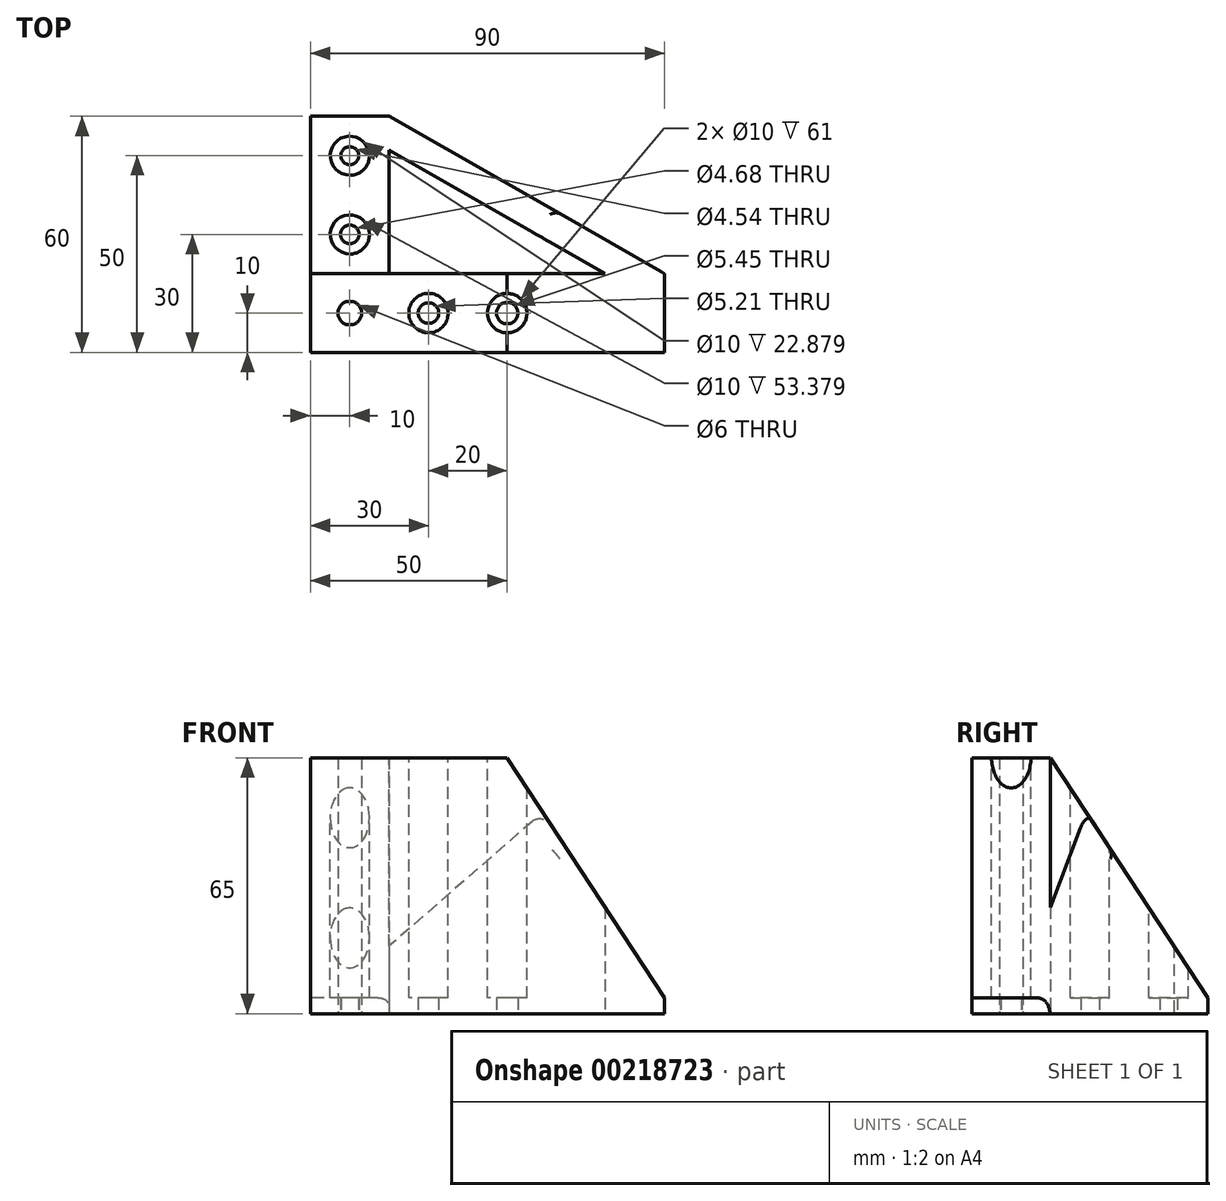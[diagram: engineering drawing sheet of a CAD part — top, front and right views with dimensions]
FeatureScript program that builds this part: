
annotation { "Feature Type Name" : "Feature", "Feature Type Description" : "" }
export const myFeature = defineFeature(function(context is Context, id is Id, definition is map)
    precondition{}
    {
        {
            var Q0;
            Q0=qCreatedBy(makeId("Top.planeOp"),FACE);
            var sketch = newSketch(context, id + "F0", { "sketchPlane" : qUnion([Q0])});
            skLineSegment(sketch, "E0", {"start": v(0, 0) * mm, "end": v(0, 60) * mm});
            skLineSegment(sketch, "E1", {"start": v(0, 60) * mm, "end": v(20, 60) * mm});
            skLineSegment(sketch, "E2", {"start": v(0, 0) * mm, "end": v(90, 0) * mm});
            skLineSegment(sketch, "E3", {"start": v(90, 0) * mm, "end": v(90, 20) * mm});
            skLineSegment(sketch, "E4", {"start": v(20, 60) * mm, "end": v(90, 20) * mm});
            skLineSegment(sketch, "E5", {"start": v(20, 20) * mm, "end": v(20, 51.36) * mm});
            skLineSegment(sketch, "E6", {"start": v(20, 51.36) * mm, "end": v(74.88, 20) * mm});
            skLineSegment(sketch, "E7", {"start": v(74.88, 20) * mm, "end": v(20, 20) * mm});
            skSolve(sketch);
        }
        {
            var Q0;
            Q0=qSketchRegion(id+"F0",true);
            extrude(context, id + "F1", {"entities" : qUnion([Q0]), "depth" : 65 * mm});
        }
        {
            var Q0;
            Q0=makeQuery(id+"F1.opExtrude","SWEPT_FACE",FACE,{"disambiguationData":[OSD([sQuery(id+"F0.wireOp",EDGE,"E2")])]});
            var sketch = newSketch(context, id + "F2", { "sketchPlane" : qUnion([Q0])});
            skLineSegment(sketch, "E8", {"start": v(50, 65) * mm, "end": v(90, 4) * mm});
            skLineSegment(sketch, "E9", {"start": v(90, 4) * mm, "end": v(90, 65) * mm});
            skLineSegment(sketch, "E10", {"start": v(90, 65) * mm, "end": v(50, 65) * mm});
            skSolve(sketch);
        }
        {
            var Q0;
            Q0=qSketchRegion(id+"F2",true);
            extrude(context, id + "F3", {"entities" : qUnion([Q0]), "operationType" : NewBodyOperationType.REMOVE, "endBound" : BoundingType.THROUGH_ALL, "oppositeDirection" : true, "depth" : 25 * mm});
        }
        {
            var Q0;
            Q0=makeQuery(id+"F1.opExtrude","SWEPT_FACE",FACE,{"disambiguationData":[OSD([sQuery(id+"F0.wireOp",EDGE,"E0")])]});
            var sketch = newSketch(context, id + "F4", { "sketchPlane" : qUnion([Q0])});
            skLineSegment(sketch, "E11", {"start": v(-60, 4) * mm, "end": v(-20, 65) * mm});
            skLineSegment(sketch, "E12", {"start": v(-20, 65) * mm, "end": v(-60, 65) * mm});
            skLineSegment(sketch, "E13", {"start": v(-60, 65) * mm, "end": v(-60, 4) * mm});
            skSolve(sketch);
        }
        {
            var Q0;
            Q0=qSketchRegion(id+"F4",true);
            extrude(context, id + "F5", {"entities" : qUnion([Q0]), "operationType" : NewBodyOperationType.REMOVE, "endBound" : BoundingType.THROUGH_ALL, "oppositeDirection" : true, "depth" : 25 * mm});
        }
        {
            var Q0;
            Q0=makeQuery(id+"F1.opExtrude","CAP_FACE",FACE,{"disambiguationData":[OSD([sQuery(id+"F0.wireOp",EDGE,"E0"),sQuery(id+"F0.wireOp",EDGE,"E1"),sQuery(id+"F0.wireOp",EDGE,"E2"),sQuery(id+"F0.wireOp",EDGE,"E3"),sQuery(id+"F0.wireOp",EDGE,"E4"),sQuery(id+"F0.wireOp",EDGE,"mdH7xUEh-kj0j-FzDd-vFJF-Ez3bFDuHEaMy"),sQuery(id+"F0.wireOp",EDGE,"4d57907b-b922-4928-aa1d-d9501c8b047b0.MirrorCS"),sQuery(id+"F0.wireOp",EDGE,"GoayG3HE-BG0Y-PVgY-aGZj-s7U7ja6lUwcO"),sQuery(id+"F0.wireOp",EDGE,"S14YtGU4-LqZk-oQQI-01Mi-7A5jnYNGNibG"),sQuery(id+"F0.wireOp",EDGE,"etAqa9y3-Zd5w-nI5t-Bn0a-wnxTIQmUJfjK"),sQuery(id+"F0.wireOp",EDGE,"WpbV4EXd-Zgvc-VK6q-gld7-0orCnQnwV1Qf")])],"isStart":true});
            var sketch = newSketch(context, id + "F6", { "sketchPlane" : qUnion([Q0])});
            skCircle(sketch, "E14", {"center": v(10, -10) * mm, "radius": 2.5 * mm});
            skCircle(sketch, "E15", {"center": v(30, -10) * mm, "radius": 2.6 * mm});
            skCircle(sketch, "E16", {"center": v(50, -10) * mm, "radius": 2.73 * mm});
            skCircle(sketch, "E17", {"center": v(10, -30) * mm, "radius": 2.34 * mm});
            skCircle(sketch, "E18", {"center": v(10, -50) * mm, "radius": 2.27 * mm});
            skSolve(sketch);
        }
        {
            var Q0;
            Q0=qSketchRegion(id+"F6",true);
            extrude(context, id + "F7", {"entities" : qUnion([Q0]), "operationType" : NewBodyOperationType.REMOVE, "endBound" : BoundingType.THROUGH_ALL, "oppositeDirection" : true, "depth" : 25 * mm});
        }
        {
            var Q0;
            Q0=makeQuery(id+"F1.opExtrude","CAP_FACE",FACE,{"disambiguationData":[OSD([sQuery(id+"F0.wireOp",EDGE,"E0"),sQuery(id+"F0.wireOp",EDGE,"E1"),sQuery(id+"F0.wireOp",EDGE,"E2"),sQuery(id+"F0.wireOp",EDGE,"E3"),sQuery(id+"F0.wireOp",EDGE,"E4"),sQuery(id+"F0.wireOp",EDGE,"mdH7xUEh-kj0j-FzDd-vFJF-Ez3bFDuHEaMy"),sQuery(id+"F0.wireOp",EDGE,"4d57907b-b922-4928-aa1d-d9501c8b047b0.MirrorCS"),sQuery(id+"F0.wireOp",EDGE,"GoayG3HE-BG0Y-PVgY-aGZj-s7U7ja6lUwcO"),sQuery(id+"F0.wireOp",EDGE,"S14YtGU4-LqZk-oQQI-01Mi-7A5jnYNGNibG"),sQuery(id+"F0.wireOp",EDGE,"etAqa9y3-Zd5w-nI5t-Bn0a-wnxTIQmUJfjK"),sQuery(id+"F0.wireOp",EDGE,"WpbV4EXd-Zgvc-VK6q-gld7-0orCnQnwV1Qf")])],"isStart":false});
            var sketch = newSketch(context, id + "F8", { "sketchPlane" : qUnion([Q0])});
            skCircle(sketch, "E19.0", {"center": v(10, 50) * mm, "radius": 2.27 * mm, "construction": true});
            skCircle(sketch, "E20.0", {"center": v(10, 30) * mm, "radius": 2.34 * mm, "construction": true});
            skCircle(sketch, "E21.0", {"center": v(10, 10) * mm, "radius": 2.5 * mm, "construction": true});
            skCircle(sketch, "E22.0", {"center": v(30, 10) * mm, "radius": 2.6 * mm, "construction": true});
            skCircle(sketch, "E23.0", {"center": v(50, 10) * mm, "radius": 2.73 * mm, "construction": true});
            skCircle(sketch, "E24", {"center": v(30, 10) * mm, "radius": 5 * mm});
            skCircle(sketch, "E25", {"center": v(50, 10) * mm, "radius": 5 * mm});
            skCircle(sketch, "E26", {"center": v(10, 30) * mm, "radius": 5 * mm});
            skCircle(sketch, "E27", {"center": v(10, 50) * mm, "radius": 5 * mm});
            skSolve(sketch);
        }
        {
            var Q0;
            Q0=qSketchRegion(id+"F8",true);
            extrude(context, id + "F9", {"entities" : qUnion([Q0]), "operationType" : NewBodyOperationType.REMOVE, "oppositeDirection" : true, "depth" : 61 * mm});
        }
        {
            var Q0;
            Q0=makeQuery(id+"F3.boolean.opBoolean","INTERSECT",EDGE,{"derivedFrom":[makeQuery(id+"F1.opExtrude","SWEPT_FACE",FACE,{"disambiguationData":[OSD([sQuery(id+"F0.wireOp",EDGE,"E4")])]}),makeQuery(id+"F3.opExtrude","SWEPT_FACE",FACE,{"disambiguationData":[OSD([sQuery(id+"F2.wireOp",EDGE,"E8")])]})]});
            var Q1;
            Q1=makeQuery(id+"F5.boolean.opBoolean","INTERSECT",EDGE,{"derivedFrom":[makeQuery(id+"F1.opExtrude","SWEPT_FACE",FACE,{"disambiguationData":[OSD([sQuery(id+"F0.wireOp",EDGE,"E4")])]}),makeQuery(id+"F5.opExtrude","SWEPT_FACE",FACE,{"disambiguationData":[OSD([sQuery(id+"F4.wireOp",EDGE,"E11")])]})]});
            var Q2;
            Q2=makeQuery(id+"F3.boolean.opBoolean","COPY",EDGE,{"derivedFrom":makeQuery(id+"F3.opExtrude","SWEPT_EDGE",EDGE,{"disambiguationData":[OSD([sQuery(id+"F0.wireOp",EDGE,"E2"),sQuery(id+"F0.wireOp",EDGE,"E3"),sQuery(id+"F2.wireOp",EDGE,"E8"),sQuery(id+"F2.wireOp",EDGE,"E9")])]})});
            var Q3;
            Q3=makeQuery(id+"F5.boolean.opBoolean","COPY",EDGE,{"derivedFrom":makeQuery(id+"F5.opExtrude","SWEPT_EDGE",EDGE,{"disambiguationData":[OSD([sQuery(id+"F0.wireOp",EDGE,"E0"),sQuery(id+"F0.wireOp",EDGE,"E1"),sQuery(id+"F4.wireOp",EDGE,"E11"),sQuery(id+"F4.wireOp",EDGE,"E13")])]})});
            var Q4;
            Q4=makeQuery(id+"F5.boolean.opBoolean","INTERSECT",EDGE,{"derivedFrom":[makeQuery(id+"F3.boolean.opBoolean","COPY",FACE,{"derivedFrom":makeQuery(id+"F3.opExtrude","SWEPT_FACE",FACE,{"disambiguationData":[OSD([sQuery(id+"F2.wireOp",EDGE,"E8")])]})}),makeQuery(id+"F5.opExtrude","SWEPT_FACE",FACE,{"disambiguationData":[OSD([sQuery(id+"F4.wireOp",EDGE,"E11")])]})]});
            fillet(context, id + "F10", {"entities" : qUnion([Q0, Q1, Q2, Q3, Q4]), "radius" : 5 * mm, "tangentPropagation" : true, "allowEdgeOverflow" : false});
        }
        {
            var Q0;
            Q0=makeQuery(id+"F1.opExtrude","CAP_FACE",FACE,{"disambiguationData":[OSD([sQuery(id+"F0.wireOp",EDGE,"E0"),sQuery(id+"F0.wireOp",EDGE,"E1"),sQuery(id+"F0.wireOp",EDGE,"E2"),sQuery(id+"F0.wireOp",EDGE,"E3"),sQuery(id+"F0.wireOp",EDGE,"E4"),sQuery(id+"F0.wireOp",EDGE,"mdH7xUEh-kj0j-FzDd-vFJF-Ez3bFDuHEaMy"),sQuery(id+"F0.wireOp",EDGE,"4d57907b-b922-4928-aa1d-d9501c8b047b0.MirrorCS"),sQuery(id+"F0.wireOp",EDGE,"GoayG3HE-BG0Y-PVgY-aGZj-s7U7ja6lUwcO"),sQuery(id+"F0.wireOp",EDGE,"S14YtGU4-LqZk-oQQI-01Mi-7A5jnYNGNibG"),sQuery(id+"F0.wireOp",EDGE,"etAqa9y3-Zd5w-nI5t-Bn0a-wnxTIQmUJfjK"),sQuery(id+"F0.wireOp",EDGE,"WpbV4EXd-Zgvc-VK6q-gld7-0orCnQnwV1Qf")])],"isStart":true});
            var sketch = newSketch(context, id + "F11", { "sketchPlane" : qUnion([Q0])});
            skCircle(sketch, "E28", {"center": v(10, -10) * mm, "radius": 3 * mm});
            skSolve(sketch);
        }
        {
            var Q0;
            Q0=qSketchRegion(id+"F11",true);
            extrude(context, id + "F12", {"entities" : qUnion([Q0]), "operationType" : NewBodyOperationType.REMOVE, "endBound" : BoundingType.THROUGH_ALL, "oppositeDirection" : true, "depth" : 25 * mm});
        }
    });
